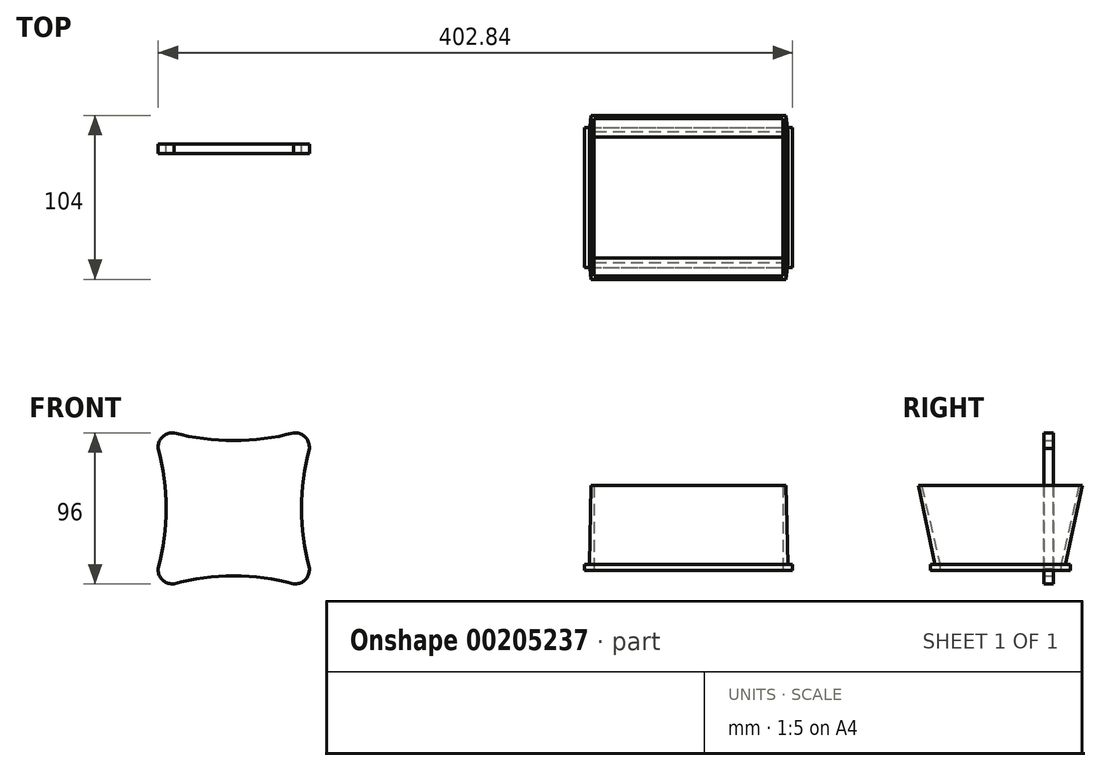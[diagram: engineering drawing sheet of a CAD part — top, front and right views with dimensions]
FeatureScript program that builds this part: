
annotation { "Feature Type Name" : "Feature", "Feature Type Description" : "" }
export const myFeature = defineFeature(function(context is Context, id is Id, definition is map)
    precondition{}
    {
        {
            var Q0;
            Q0=qCreatedBy(makeId("Front.planeOp"),FACE);
            var sketch = newSketch(context, id + "F0", { "sketchPlane" : qUnion([Q0])});
            skLineSegment(sketch, "E0.bottom", {"start": v(-29.77, -8.46) * mm, "end": v(-28.77, -8.46) * mm});
            skLineSegment(sketch, "E0.top", {"start": v(-29.77, 87.54) * mm, "end": v(-28.77, 87.54) * mm});
            skLineSegment(sketch, "E0.left", {"start": v(-38.77, 0.54) * mm, "end": v(-38.77, 1.54) * mm});
            skLineSegment(sketch, "E0.right", {"start": v(57.23, 0.54) * mm, "end": v(57.23, 1.54) * mm});
            skArc(sketch, "E1", {"start": v(-28.77, 87.54) * mm, "mid": v(9.23, 82.54) * mm, "end": v(47.23, 87.54) * mm});
            skPoint(sketch, "E1.centerSnap0", {"position": v(9.23, 87.54) * mm});
            skLineSegment(sketch, "E2", {"start": v(-28.77, 87.54) * mm, "end": v(-28.77, 95.12) * mm, "construction": true});
            skLineSegment(sketch, "E3.trimOffspring", {"start": v(47.23, 87.54) * mm, "end": v(48.23, 87.54) * mm});
            skArc(sketch, "E4.1.0", {"start": v(-38.77, 1.54) * mm, "mid": v(-33.77, 39.54) * mm, "end": v(-38.77, 77.54) * mm});
            skArc(sketch, "E4.2.0", {"start": v(47.23, -8.46) * mm, "mid": v(9.23, -3.46) * mm, "end": v(-28.77, -8.46) * mm});
            skArc(sketch, "E4.3.0", {"start": v(57.23, 77.54) * mm, "mid": v(52.23, 39.54) * mm, "end": v(57.23, 1.54) * mm});
            skPoint(sketch, "E4.center", {"position": v(9.23, 39.54) * mm});
            skLineSegment(sketch, "E5.trimOffspring", {"start": v(-38.77, 77.54) * mm, "end": v(-38.77, 78.54) * mm});
            skLineSegment(sketch, "E6.trimOffspring", {"start": v(47.23, -8.46) * mm, "end": v(48.23, -8.46) * mm});
            skLineSegment(sketch, "E7.trimOffspring", {"start": v(57.23, 77.54) * mm, "end": v(57.23, 78.54) * mm});
            skPoint(sketch, "E8.visualSharp", {"position": v(-38.77, 87.54) * mm});
            skArc(sketch, "E8.filletArc", {"start": v(-29.77, 87.54) * mm, "mid": v(-36.13, 84.9) * mm, "end": v(-38.77, 78.54) * mm});
            skPoint(sketch, "E9.visualSharp", {"position": v(57.23, 87.54) * mm});
            skArc(sketch, "E9.filletArc", {"start": v(57.23, 78.54) * mm, "mid": v(54.6, 84.9) * mm, "end": v(48.23, 87.54) * mm});
            skPoint(sketch, "E10.visualSharp", {"position": v(57.23, -8.46) * mm});
            skArc(sketch, "E10.filletArc", {"start": v(48.23, -8.46) * mm, "mid": v(54.6, -5.83) * mm, "end": v(57.23, 0.54) * mm});
            skPoint(sketch, "E11.visualSharp", {"position": v(-38.77, -8.46) * mm});
            skArc(sketch, "E11.filletArc", {"start": v(-38.77, 0.54) * mm, "mid": v(-36.13, -5.83) * mm, "end": v(-29.77, -8.46) * mm});
            skSolve(sketch);
        }
        {
            var Q0;
            Q0=makeQuery(id+"F0.imprint","IMPRINT",FACE,{"disambiguationData":[TD([[makeQuery(id+"F0.imprint","IMPRINT",EDGE,{"derivedFrom":sQuery(id+"F0.wireOp",EDGE,"E0.bottom")}),1.0]])]});
            extrude(context, id + "F1", {"entities" : qUnion([Q0]), "depth" : 6 * mm});
        }
        {
            var Q0;
            Q0=qCreatedBy(makeId("Top.planeOp"),FACE);
            var sketch = newSketch(context, id + "F2", { "sketchPlane" : qUnion([Q0])});
            skLineSegment(sketch, "E12.bottom", {"start": v(238.07, 4.73) * mm, "end": v(358.07, 4.73) * mm});
            skLineSegment(sketch, "E12.top", {"start": v(238.07, -72.27) * mm, "end": v(358.07, -72.27) * mm});
            skLineSegment(sketch, "E12.left", {"start": v(238.07, 4.73) * mm, "end": v(238.07, -72.27) * mm});
            skLineSegment(sketch, "E12.right", {"start": v(358.07, 4.73) * mm, "end": v(358.07, -72.27) * mm});
            skLineSegment(sketch, "E13.bottom", {"start": v(232.07, 10.73) * mm, "end": v(364.07, 10.73) * mm});
            skLineSegment(sketch, "E13.top", {"start": v(232.07, -78.27) * mm, "end": v(364.07, -78.27) * mm});
            skLineSegment(sketch, "E13.left", {"start": v(232.07, 10.73) * mm, "end": v(232.07, -78.27) * mm});
            skLineSegment(sketch, "E13.right", {"start": v(364.07, 10.73) * mm, "end": v(364.07, -78.27) * mm});
            skSolve(sketch);
        }
        {
            var Q0;
            Q0 = qSketchRegion(id + "F2", true);
            extrude(context, id + "F3", {"entities" : qUnion([Q0]), "depth" : 4 * mm});
        }
        {
            var Q0;
            Q0=makeQuery(id+"F3.opExtrude","CAP_FACE",FACE,{"disambiguationData":[OSD([sQuery(id+"F2.wireOp",EDGE,"E12.bottom"),sQuery(id+"F2.wireOp",EDGE,"E12.top"),sQuery(id+"F2.wireOp",EDGE,"E12.left"),sQuery(id+"F2.wireOp",EDGE,"E12.right"),sQuery(id+"F2.wireOp",EDGE,"E13.bottom"),sQuery(id+"F2.wireOp",EDGE,"E13.top"),sQuery(id+"F2.wireOp",EDGE,"E13.left"),sQuery(id+"F2.wireOp",EDGE,"E13.right")])],"isStart":false});
            cPlane(context, id + "F4", {"entities" : qUnion([Q0]), "cplaneType" : CPlaneType.OFFSET, "offset" : 50 * mm, "width" : 150 * mm, "height" : 150 * mm});
        }
        {
            var Q0;
            Q0=qCreatedBy(id+"F4.planeOp",FACE);
            var sketch = newSketch(context, id + "F5", { "sketchPlane" : qUnion([Q0])});
            skLineSegment(sketch, "E14.bottom", {"start": v(236.07, 18.23) * mm, "end": v(360.07, 18.23) * mm});
            skLineSegment(sketch, "E14.top", {"start": v(236.07, -85.77) * mm, "end": v(360.07, -85.77) * mm});
            skLineSegment(sketch, "E14.left", {"start": v(236.07, 18.23) * mm, "end": v(236.07, -85.77) * mm});
            skLineSegment(sketch, "E14.right", {"start": v(360.07, 18.23) * mm, "end": v(360.07, -85.77) * mm});
            skSolve(sketch);
        }
        {
            var Q0;
            Q0=makeQuery(id+"F3.opExtrude","CAP_FACE",FACE,{"disambiguationData":[OSD([sQuery(id+"F2.wireOp",EDGE,"E12.bottom"),sQuery(id+"F2.wireOp",EDGE,"E12.top"),sQuery(id+"F2.wireOp",EDGE,"E12.left"),sQuery(id+"F2.wireOp",EDGE,"E12.right"),sQuery(id+"F2.wireOp",EDGE,"E13.bottom"),sQuery(id+"F2.wireOp",EDGE,"E13.top"),sQuery(id+"F2.wireOp",EDGE,"E13.left"),sQuery(id+"F2.wireOp",EDGE,"E13.right")])],"isStart":false});
            var sketch = newSketch(context, id + "F6", { "sketchPlane" : qUnion([Q0])});
            skLineSegment(sketch, "E15.bottom", {"start": v(361.07, 7.73) * mm, "end": v(235.07, 7.73) * mm});
            skLineSegment(sketch, "E15.top", {"start": v(361.07, -75.27) * mm, "end": v(235.07, -75.27) * mm});
            skLineSegment(sketch, "E15.left", {"start": v(361.07, 7.73) * mm, "end": v(361.07, -75.27) * mm});
            skLineSegment(sketch, "E15.right", {"start": v(235.07, 7.73) * mm, "end": v(235.07, -75.27) * mm});
            skSolve(sketch);
        }
        {
            var Q1;
            Q1 = qSketchRegion(id + "F5", true);
            var Q2;
            Q2 = qSketchRegion(id + "F6", true);
            loft(context, id + "F7", {"operationType" : NewBodyOperationType.ADD, "sheetProfilesArray" : [{ "sheetProfileEntities" : qUnion([Q1]) }, { "sheetProfileEntities" : qUnion([Q2]) }]});
        }
        {
            var Q0;
            Q0=makeQuery(id+"F5.imprint","IMPRINT",FACE,{"disambiguationData":[TD([[makeQuery(id+"F5.imprint","IMPRINT",EDGE,{"derivedFrom":sQuery(id+"F5.wireOp",EDGE,"E14.bottom")}),-1.0]])]});
            var sketch = newSketch(context, id + "F8", { "sketchPlane" : qUnion([Q0])});
            skLineSegment(sketch, "E16.bottom", {"start": v(238.07, 16.23) * mm, "end": v(358.07, 16.23) * mm});
            skLineSegment(sketch, "E16.top", {"start": v(238.07, -83.77) * mm, "end": v(358.07, -83.77) * mm});
            skLineSegment(sketch, "E16.left", {"start": v(238.07, 16.23) * mm, "end": v(238.07, -83.77) * mm});
            skLineSegment(sketch, "E16.right", {"start": v(358.07, 16.23) * mm, "end": v(358.07, -83.77) * mm});
            skSolve(sketch);
        }
        {
            var Q1;
            Q1 = qSketchRegion(id + "F8", true);
            var Q2;
            Q2=makeQuery(id+"F7.opLoft","CAP_FACE",FACE,{"disambiguationData":[OSD([makeQuery(id+"F6.imprint","IMPRINT",FACE,{"disambiguationData":[TD([[makeQuery(id+"F6.imprint","IMPRINT",EDGE,{"derivedFrom":sQuery(id+"F6.wireOp",EDGE,"E15.bottom")}),1.0]])]})])],"isStart":true});
            loft(context, id + "F9", {"operationType" : NewBodyOperationType.REMOVE, "sheetProfilesArray" : [{ "sheetProfileEntities" : qUnion([Q1]) }, { "sheetProfileEntities" : qUnion([Q2]) }]});
        }
    });
